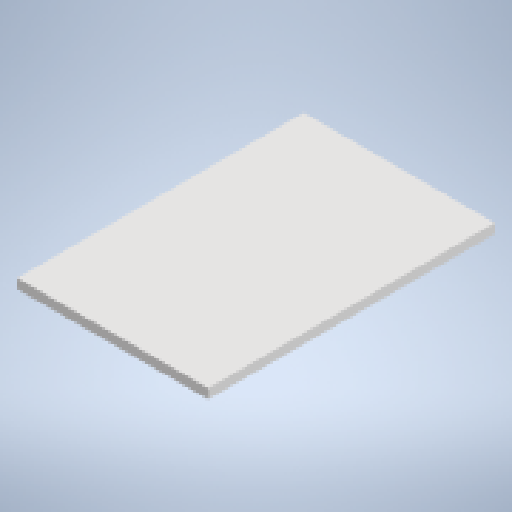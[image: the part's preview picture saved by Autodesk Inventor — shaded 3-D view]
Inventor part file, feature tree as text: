
AUTODESK INVENTOR PART (.ipt)
format: ipt  version: 2023 (Build 270158000, 158)  size: 146,944 bytes
history: native  units: mm
features: reference x11, other x4, extrude x3, sketch x3
ambient origin geometry x8: Origin, YZ Plane, XZ Plane, XY Plane, X Axis, Y Axis, Z Axis, Center Point
bodies: Solid1 (feature_tree)
feature tree (21):
  other  "<userpath>\OneDrive\ClawdDrive\Objet3D\IminaProbe\Settings.xlsx"
  extrude  "Extrusion1"  Depth=100.0mm
  extrude  "Extrusion2"  TaperAngle=0.0deg  [1 undecoded]
  extrude  "Extrusion3"  TaperAngle=0.0deg  [1 undecoded]
  sketch  "Sketch1"  dims[d0=150.0mm d1=100.0mm]
  sketch  "Sketch2"  dims[d2=5.0mm d3=0.0mm]
  reference  "Reference1"
  reference  "Reference2"
  reference  "Reference3"
  reference  "Reference4"
  reference  "Reference5"
  reference  "Reference6"
  reference  "Reference7"
  reference  "Reference8"
  sketch  "Sketch3"  dims[d4=5.0mm d5=0.0mm d6=5.0mm d7=0.0mm]
  reference  "Reference9"
  reference  "Reference10"
  reference  "Reference11"
  other  "<userpath>\OneDrive\ClawdDrive\Objet3D\IminaProbe\Flex.iam"
  other  "Flex.iam"
  other  "FlexBlocWheel:1"
note: 2 required parameter values undecoded (feature->parameter linkage not recoverable at this tier; creation-order binding heuristic only, values carry confidence <= 0.55)
